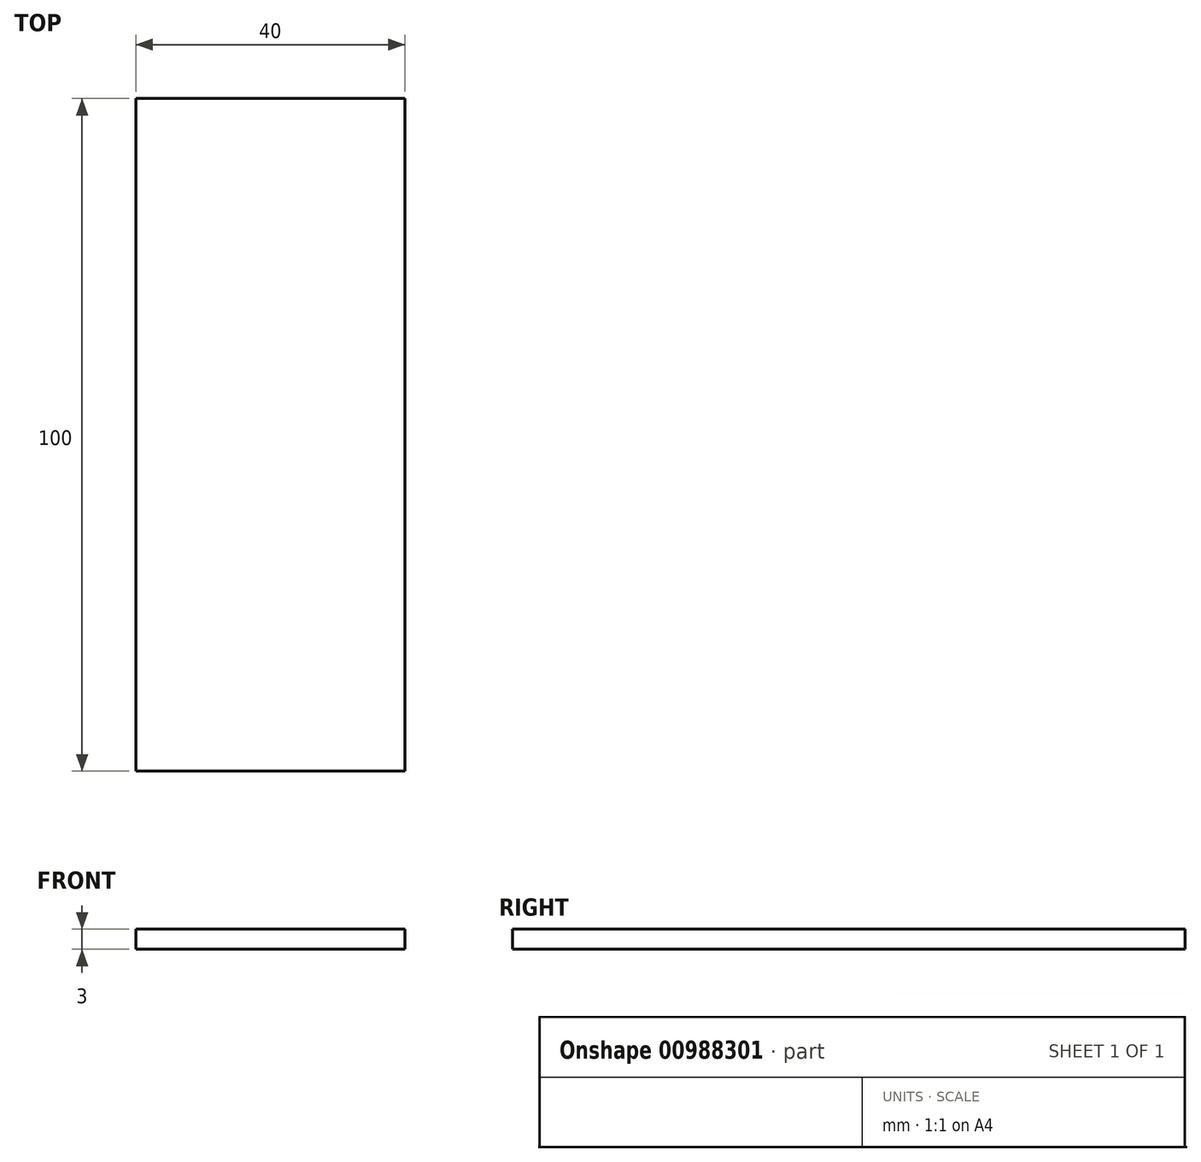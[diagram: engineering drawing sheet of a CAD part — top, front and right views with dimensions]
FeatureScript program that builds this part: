
annotation { "Feature Type Name" : "Feature", "Feature Type Description" : "" }
export const myFeature = defineFeature(function(context is Context, id is Id, definition is map)
    precondition{}
    {
        {
            var Q0;
            Q0=qCreatedBy(makeId("Top.planeOp"),FACE);
            var sketch = newSketch(context, id + "F0", { "sketchPlane" : qUnion([Q0])});
            skLineSegment(sketch, "E0.bottom", {"start": v(0, 0) * mm, "end": v(40, 0) * mm});
            skLineSegment(sketch, "E0.top", {"start": v(0, 100) * mm, "end": v(40, 100) * mm});
            skLineSegment(sketch, "E0.left", {"start": v(0, 0) * mm, "end": v(0, 100) * mm});
            skLineSegment(sketch, "E0.right", {"start": v(40, 0) * mm, "end": v(40, 100) * mm});
            skSolve(sketch);
        }
        {
            var Q0;
            Q0=makeQuery(id+"F0.imprint","IMPRINT",FACE,{"disambiguationData":[TD([[makeQuery(id+"F0.imprint","IMPRINT",EDGE,{"derivedFrom":sQuery(id+"F0.wireOp",EDGE,"E0.bottom")}),1.0]])]});
            extrude(context, id + "F1", {"entities" : qUnion([Q0]), "oppositeDirection" : true, "depth" : 3 * mm, "offsetDistance" : 25 * mm});
        }
    });
